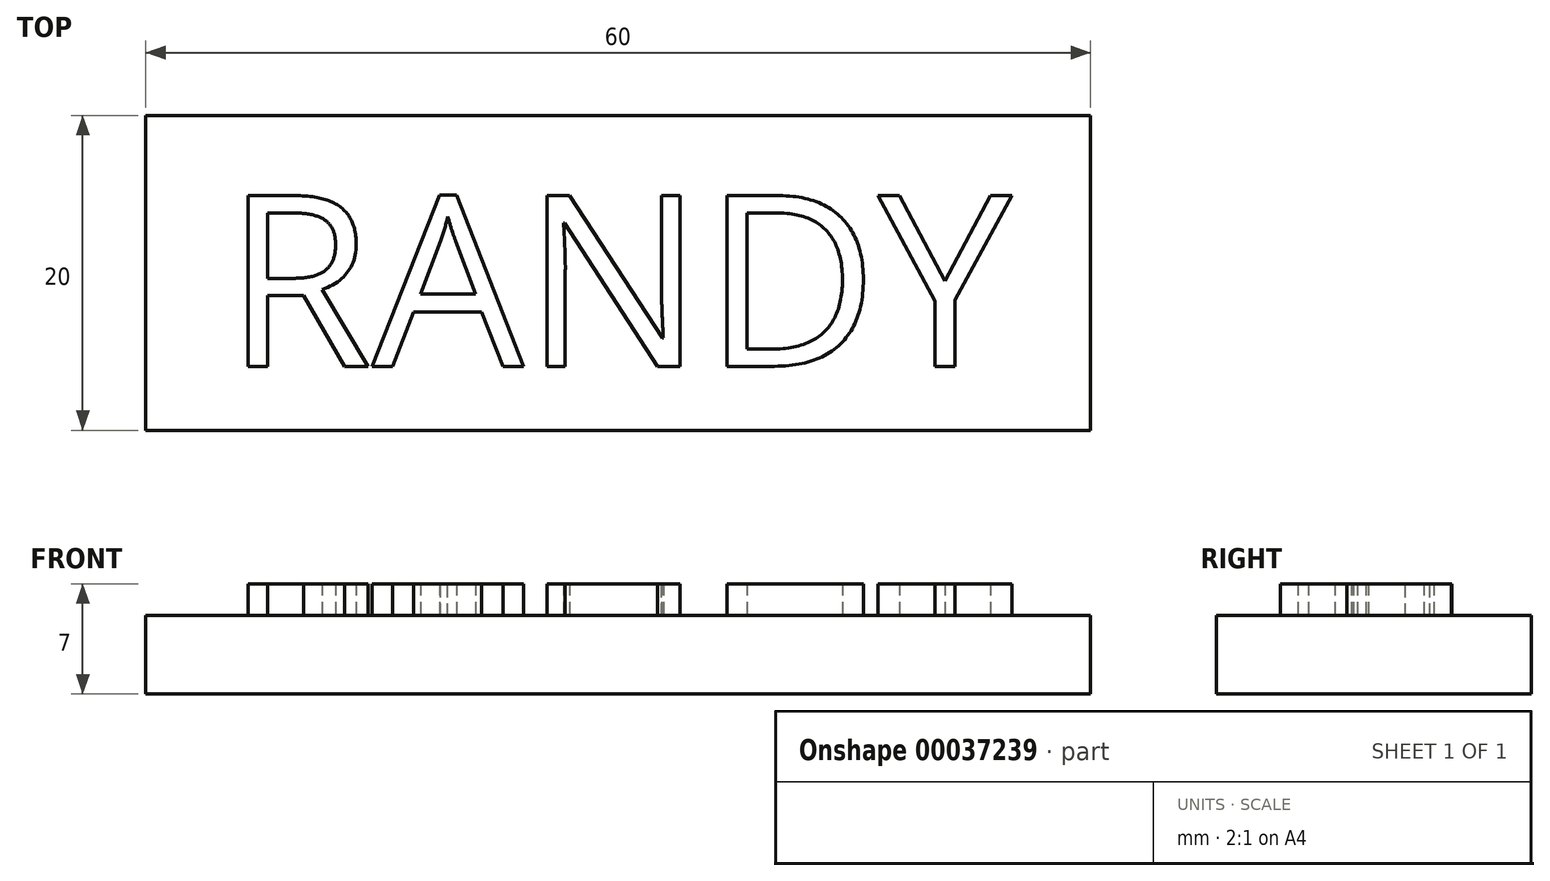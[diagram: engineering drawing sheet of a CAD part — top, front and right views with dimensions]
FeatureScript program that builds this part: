
annotation { "Feature Type Name" : "Feature", "Feature Type Description" : "" }
export const myFeature = defineFeature(function(context is Context, id is Id, definition is map)
    precondition{}
    {
        {
            var Q0;
            Q0=qCreatedBy(makeId("Top.planeOp"),FACE);
            var sketch = newSketch(context, id + "F0", { "sketchPlane" : qUnion([Q0])});
            skLineSegment(sketch, "E0.rect.bottom", {"start": v(30, 10) * mm, "end": v(-30, 10) * mm});
            skLineSegment(sketch, "E0.rect.top", {"start": v(30, -10) * mm, "end": v(-30, -10) * mm});
            skLineSegment(sketch, "E0.rect.left", {"start": v(30, 10) * mm, "end": v(30, -10) * mm});
            skLineSegment(sketch, "E0.rect.right", {"start": v(-30, 10) * mm, "end": v(-30, -10) * mm});
            skPoint(sketch, "E0.rect.middle", {"position": v(0, 0) * mm});
            skSolve(sketch);
        }
        {
            var Q0;
            Q0 = qSketchRegion(id + "F0", true);
            extrude(context, id + "F1", {"entities" : qUnion([Q0]), "depth" : 5 * mm});
        }
        {
            var Q0;
            Q0=makeQuery(id+"F1.opExtrude","CAP_FACE",FACE,{"disambiguationData":[OSD([sQuery(id+"F0.wireOp",EDGE,"E0.rect.bottom"),sQuery(id+"F0.wireOp",EDGE,"E0.rect.top"),sQuery(id+"F0.wireOp",EDGE,"E0.rect.left"),sQuery(id+"F0.wireOp",EDGE,"E0.rect.right")])],"isStart":false});
            var sketch = newSketch(context, id + "F2", { "sketchPlane" : qUnion([Q0])});
            skText(sketch, "E1", { "text": "RANDY", "fontName": "OpenSans-Regular.ttf"});
            const initialGuessF2  = {"E1": [-0.025, -0.00593, 1, 0, 0.01093]};
            skSetInitialGuess(sketch, initialGuessF2);
            skSolve(sketch);
        }
        {
            var Q0;
            Q0 = qSketchRegion(id + "F2", true);
            extrude(context, id + "F3", {"entities" : qUnion([Q0]), "operationType" : NewBodyOperationType.ADD, "depth" : 2 * mm});
        }
    });
